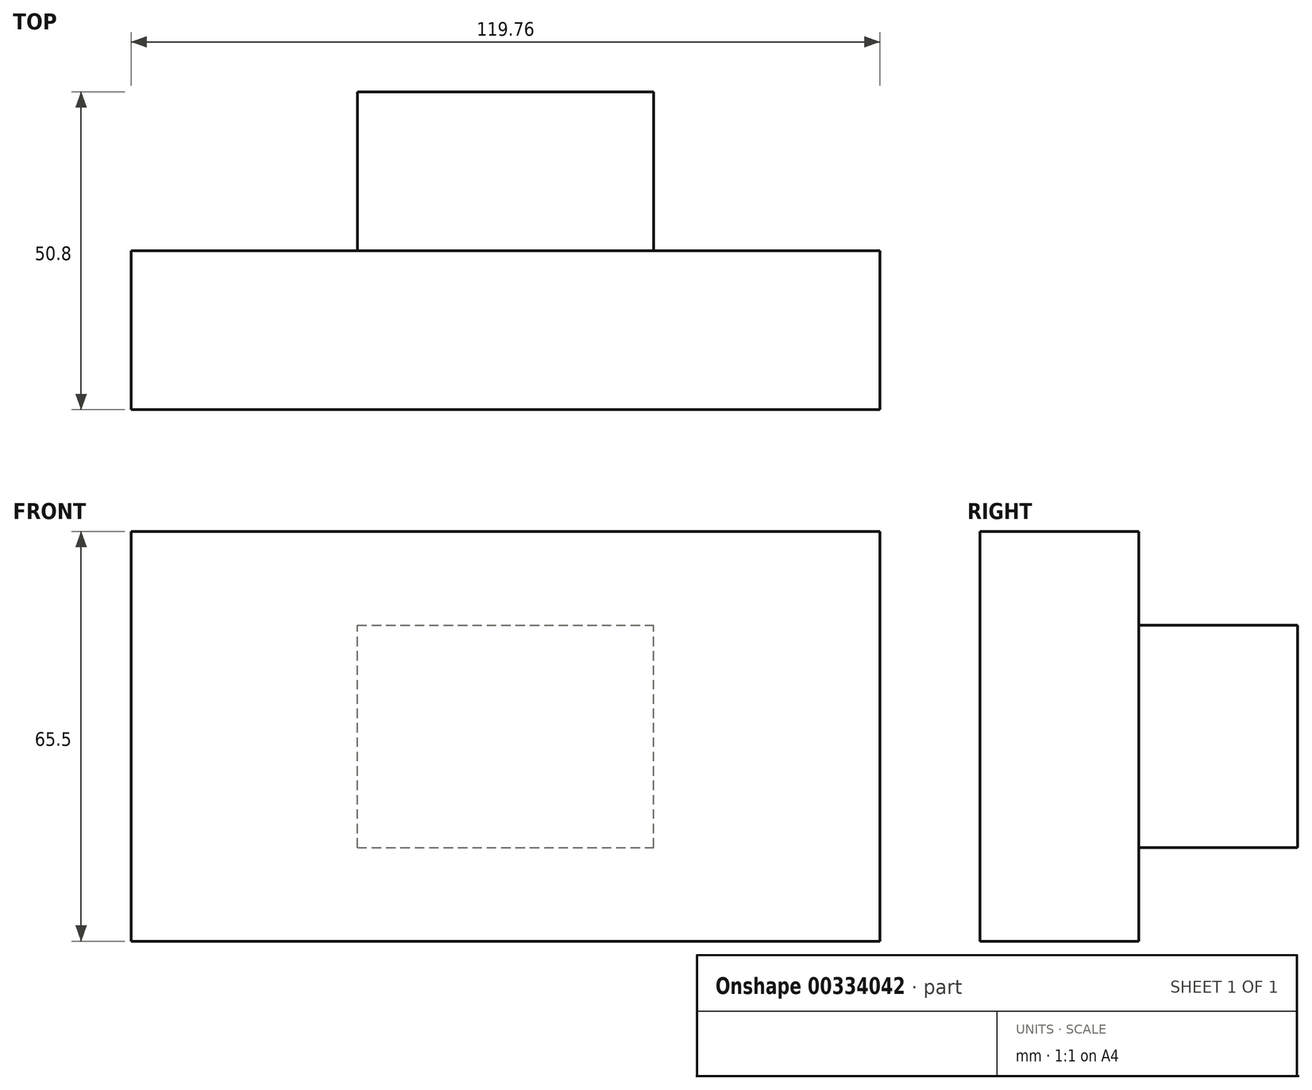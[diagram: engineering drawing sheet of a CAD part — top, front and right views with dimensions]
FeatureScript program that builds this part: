
annotation { "Feature Type Name" : "Feature", "Feature Type Description" : "" }
export const myFeature = defineFeature(function(context is Context, id is Id, definition is map)
    precondition{}
    {
        {
            var Q0;
            Q0=qCreatedBy(makeId("Front.planeOp"),FACE);
            var sketch = newSketch(context, id + "F0", { "sketchPlane" : qUnion([Q0])});
            skLineSegment(sketch, "E0.bottom", {"start": v(-59.88, -32.75) * mm, "end": v(59.88, -32.75) * mm});
            skLineSegment(sketch, "E0.top", {"start": v(-59.88, 32.75) * mm, "end": v(59.88, 32.75) * mm});
            skLineSegment(sketch, "E0.left", {"start": v(-59.88, -32.75) * mm, "end": v(-59.88, 32.75) * mm});
            skLineSegment(sketch, "E0.right", {"start": v(59.88, -32.75) * mm, "end": v(59.88, 32.75) * mm});
            skPoint(sketch, "E0.middle", {"position": v(0, 0) * mm});
            skSolve(sketch);
        }
        {
            var Q0;
            Q0=makeQuery(id+"F0.imprint","IMPRINT",FACE,{"disambiguationData":[TD([[makeQuery(id+"F0.imprint","IMPRINT",EDGE,{"derivedFrom":sQuery(id+"F0.wireOp",EDGE,"E0.bottom")}),1.0]])]});
            extrude(context, id + "F1", {"entities" : qUnion([Q0]), "depth" : 25.4 * mm});
        }
        {
            var Q0;
            Q0=makeQuery(id+"F1.opExtrude","CAP_FACE",FACE,{"disambiguationData":[OSD([sQuery(id+"F0.wireOp",EDGE,"E0.bottom"),sQuery(id+"F0.wireOp",EDGE,"E0.top"),sQuery(id+"F0.wireOp",EDGE,"E0.left"),sQuery(id+"F0.wireOp",EDGE,"E0.right")])],"isStart":true});
            var sketch = newSketch(context, id + "F2", { "sketchPlane" : qUnion([Q0])});
            skLineSegment(sketch, "E1.bottom", {"start": v(23.7, -17.78) * mm, "end": v(-23.7, -17.78) * mm});
            skLineSegment(sketch, "E1.top", {"start": v(23.7, 17.78) * mm, "end": v(-23.7, 17.78) * mm});
            skLineSegment(sketch, "E1.left", {"start": v(23.7, -17.78) * mm, "end": v(23.7, 17.78) * mm});
            skLineSegment(sketch, "E1.right", {"start": v(-23.7, -17.78) * mm, "end": v(-23.7, 17.78) * mm});
            skPoint(sketch, "E1.middle", {"position": v(0, 0) * mm});
            skSolve(sketch);
        }
        {
            var Q0;
            Q0=makeQuery(id+"F2.imprint","IMPRINT",FACE,{"disambiguationData":[TD([[makeQuery(id+"F2.imprint","IMPRINT",EDGE,{"derivedFrom":sQuery(id+"F2.wireOp",EDGE,"E1.bottom")}),-1.0]])]});
            extrude(context, id + "F3", {"entities" : qUnion([Q0]), "operationType" : NewBodyOperationType.ADD, "depth" : 25.4 * mm});
        }
    });
